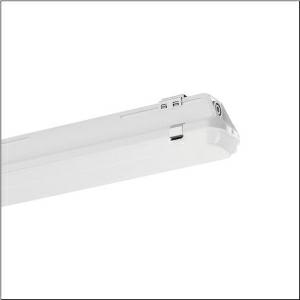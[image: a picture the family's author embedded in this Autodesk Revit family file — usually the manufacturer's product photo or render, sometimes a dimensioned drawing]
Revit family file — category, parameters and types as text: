
# Revit family: monsun_r__21_emergency_51fb10dl447k3h_80f6
name_source: partatom
category: Lighting Fixtures
units: mm (PartAtom-declared; Revit-internal decimal feet)

## family parameters
Cut with Voids When Loaded = No
Host = Face
Light Source = No
Part Type = Normal
Room Calculation Point = No
Round Connector Dimension = Use Diameter
Shared = No

## types (1)
- --- (1 x LED, 4330 lm, 28.1 W, 4000K)
    Apparent Load = 28 VA
    CIE Flux Codes = 46 76 93 94 100
    Color Rendering = 80
    Color Temperature = 4000K
    Default Elevation = 1800 mm
    Description = Monsun® 21 emergency, damp-proof luminaire, chain hanger, primary optical cover: enclosure, of PMMA, light emission: direct distribution, primary light characteristic: symmetric, installation type: vertical mounting, horizontal mounting, surface-mounted, suspended mounting, LED, rated luminous flux: 4.330lm, luminous efficacy: 178lm/W, light colour: 840, colour temperature: 4000K, control gear: DALI 2, with terminal, 5-pole, max. 2.5mm², mains connection: 220..240V, AC, 50/60Hz, rated input power: 28W, control gear: single battery element, battery: LiFePO4, 9Ah, housing, of glass-fibre reinforced plastic, uncoated, bright grey, incl. chain hanger, length: 1.299mm, width: 90mm, height: 88mm, clip for enclosure, of stainless steel (V2A), ceiling mounting element, of stainless steel (V2A), chain hanger, of stainless steel (V2A), protection rating (complete): IP66, insulation class (complete): insulation class I (protective earthing), certification: CE, UKCA, protection symbol: D, impact resistance: IK04, permissible operating ambient temperature: +5..+25°C, standard: EN 50419, EN 60598-2-1, corresponds to IFS (International Featured Standards) requirements for safety and quality in the food industry, for indoor or canopied outdoor use, no direct snow, no direct sun, no direct rain, LABS conformity tested according to VDMA 24364:2018-05, contact your sales advisor before using the luminaires in applications with unclear chemical exposure, large temperature fluctuations or condensation-forming humidity, packaging unit: 1 piece
    Height = 88 mm
    Lamp = 1 x LED
    Lamp Light Flux = 4330 lm
    Lamp Power = 28.1 W
    Lamp count = 1
    Length = 1299 mm
    Luminous efficacy = 154 lm/W
    Manufacturer = Siteco
    ModVariant = No
    Model = 51FB10DL447K3H
    Mounting Place = Ceiling
    Mounting Type = Surface mounted
    Number of Poles = 1
    OnlyDefault = Yes
    Power Factor = 1
    Product Name = Monsun® 21 emergency
    Product group = damp-proof luminaire
    ProductGroupID = 301
    Protection Class = Protection class I
    Protection Degree = IP 66
    RLX_Detail_Level = 1
    RLX_Emergency_Light_Flux = 0 lm
    RLX_Emergency_Type = 0
    RLX_Emergency_Type_DB = No
    RlxData = <blob elided: 93633 chars, md5=a09930d9>
    Socket = socket
    Standby Power = 0 W
    System Light Flux = 4330 lm
    System Power = 28 W
    Type Comments = : luminous flux: 100 % | dim-lin: 254 | 164 mA
    Type Image = l_1319656.jpg
    URL = http://relux.com
    VarID = @adj_042447
    Voltage = 0 V
    Weight = 0.00 kg
    Width = 90 mm

## geometry (parser evidence)
native form markers: Blend x4, Sweep x13
no freeform markers — native parametric forms only
